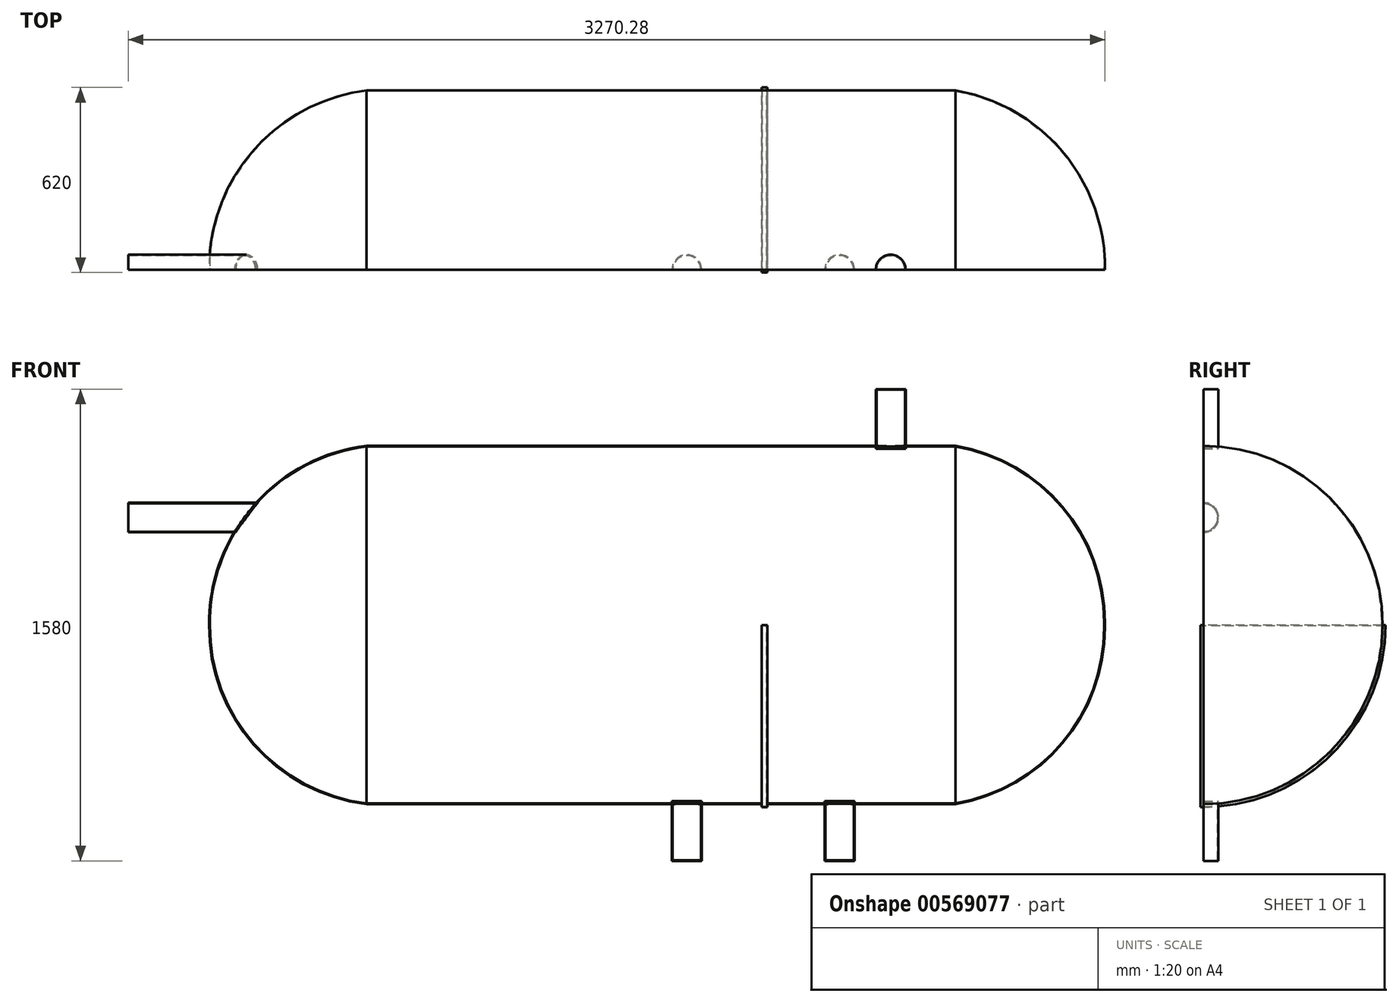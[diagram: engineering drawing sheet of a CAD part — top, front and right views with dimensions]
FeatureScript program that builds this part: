
annotation { "Feature Type Name" : "Feature", "Feature Type Description" : "" }
export const myFeature = defineFeature(function(context is Context, id is Id, definition is map)
    precondition{}
    {
        {
            var Q0;
            Q0=qCreatedBy(makeId("Front.planeOp"),FACE);
            var sketch = newSketch(context, id + "F0", { "sketchPlane" : qUnion([Q0])});
            skLineSegment(sketch, "E0.bottom", {"start": v(500, 0) * mm, "end": v(2500, 0) * mm});
            skLineSegment(sketch, "E0.top", {"start": v(500, -600) * mm, "end": v(2500, -600) * mm});
            skArc(sketch, "E1", {"start": v(0, 0) * mm, "mid": v(149.32, -400.52) * mm, "end": v(527.38, -600) * mm});
            skArc(sketch, "E2", {"start": v(2500, -600) * mm, "mid": v(2861, -392.5) * mm, "end": v(3000, 0) * mm});
            skLineSegment(sketch, "E3", {"start": v(0, 0) * mm, "end": v(500, 0) * mm});
            skLineSegment(sketch, "E4", {"start": v(2500, 0) * mm, "end": v(3000, 0) * mm});
            skSolve(sketch);
        }
        {
            var Q0;
            Q0 = qSketchRegion(id + "F0", true);
            var Q1;
            Q1=sQuery(id+"F0.wireOp",EDGE,"E0.bottom");
            revolve(context, id + "F1", {"entities" : qUnion([Q0]), "axis" : qUnion([Q1]), "revolveType" : RevolveType.ONE_DIRECTION, "angle" : 180 * degree});
        }
        {
            var Q0;
            Q0=makeQuery(id+"F1.opRevolve","CAP_FACE",FACE,{"disambiguationData":[OSD([sQuery(id+"F0.wireOp",EDGE,"E0.bottom"),sQuery(id+"F0.wireOp",EDGE,"E0.top"),sQuery(id+"F0.wireOp",EDGE,"E1"),sQuery(id+"F0.wireOp",EDGE,"E2"),sQuery(id+"F0.wireOp",EDGE,"E3"),sQuery(id+"F0.wireOp",EDGE,"E4")])],"isStart":false});
            shell(context, id + "F2", {"entities" : qUnion([Q0]), "thickness" : 2.5 * mm});
        }
        {
            var Q0;
            Q0=qCreatedBy(makeId("Front.planeOp"),FACE);
            var sketch = newSketch(context, id + "F3", { "sketchPlane" : qUnion([Q0])});
            skLineSegment(sketch, "E5", {"start": v(170.95, 360) * mm, "end": v(-279.05, 360) * mm});
            skArc(sketch, "E6", {"start": v(-420, 500) * mm, "mid": v(-378.38, 400.95) * mm, "end": v(-279.05, 360) * mm});
            skLineSegment(sketch, "E7", {"start": v(-420, 500) * mm, "end": v(-420, 900) * mm});
            skSolve(sketch);
        }
        {
            var Q0;
            Q0=qCreatedBy(makeId("Top.planeOp"),FACE);
            cPlane(context, id + "F4", {"entities" : qUnion([Q0]), "cplaneType" : CPlaneType.OFFSET, "offset" : 900 * mm, "width" : 150 * mm, "height" : 150 * mm});
        }
        {
            var Q0;
            Q0=qCreatedBy(id+"F4.planeOp",FACE);
            var sketch = newSketch(context, id + "F5", { "sketchPlane" : qUnion([Q0])});
            skCircle(sketch, "E8", {"center": v(-420, 0) * mm, "radius": 50 * mm});
            skSolve(sketch);
        }
        {
            var Q0;
            Q0=makeQuery(id+"F5.imprint","IMPRINT",FACE,{"disambiguationData":[TD([[makeQuery(id+"F5.imprint","IMPRINT",EDGE,{"derivedFrom":sQuery(id+"F5.wireOp",EDGE,"E8")}),1.0]])]});
            var Q1;
            Q1 = qConstructionFilter(qBodyType(qCreatedBy(id + "F3" ,EDGE), BodyType.WIRE), ConstructionObject.NO);
            sweep(context, id + "F6", {"profiles" : qUnion([Q0]), "path" : qUnion([Q1])});
        }
        {
            var Q0;
            Q0=qCreatedBy(makeId("Front.planeOp"),FACE);
            var sketch = newSketch(context, id + "F7", { "sketchPlane" : qUnion([Q0])});
            skLineSegment(sketch, "E9.bottom", {"start": v(1850, -610) * mm, "end": v(1870, -610) * mm});
            skLineSegment(sketch, "E9.top", {"start": v(1850, 0) * mm, "end": v(1870, 0) * mm});
            skLineSegment(sketch, "E9.left", {"start": v(1850, -610) * mm, "end": v(1850, 0) * mm});
            skLineSegment(sketch, "E9.right", {"start": v(1870, -610) * mm, "end": v(1870, 0) * mm});
            skSolve(sketch);
        }
        {
            var Q0;
            Q0 = qSketchRegion(id + "F7", true);
            var Q1;
            Q1=sQuery(id+"F7.wireOp",EDGE,"E9.top");
            revolve(context, id + "F8", {"operationType" : NewBodyOperationType.ADD, "entities" : qUnion([Q0]), "axis" : qUnion([Q1]), "revolveType" : RevolveType.ONE_DIRECTION, "angle" : 90 * degree});
        }
        {
            var Q0;
            Q0=makeQuery(id+"F66TGwe3fEh8Ifu_1.boolean.opBoolean","MERGE",FACE,{"derivedFrom":[makeQuery(id+"F8.boolean.opBoolean","MERGE",FACE,{"derivedFrom":[makeQuery(id+"F1.opRevolve","CAP_FACE",FACE,{"disambiguationData":[OSD([sQuery(id+"F0.wireOp",EDGE,"E0.bottom"),sQuery(id+"F0.wireOp",EDGE,"E0.top"),sQuery(id+"F0.wireOp",EDGE,"E1"),sQuery(id+"F0.wireOp",EDGE,"E2"),sQuery(id+"F0.wireOp",EDGE,"E3"),sQuery(id+"F0.wireOp",EDGE,"E4")])],"isStart":false}),makeQuery(id+"F8.opRevolve","CAP_FACE",FACE,{"disambiguationData":[OSD([sQuery(id+"F7.wireOp",EDGE,"E9.bottom"),sQuery(id+"F7.wireOp",EDGE,"E9.top"),sQuery(id+"F7.wireOp",EDGE,"E9.left"),sQuery(id+"F7.wireOp",EDGE,"E9.right")])],"isStart":true})]}),makeQuery(id+"F66TGwe3fEh8Ifu_1.opExtrude","CAP_FACE",FACE,{"disambiguationData":[OSD([sQuery(id+"FwUeZOf4pXkqyWq_1.wireOp",EDGE,"cfLgTzSa-ifk0-79PM-MiWR-QQtcIMDqkhwK.bottom"),sQuery(id+"FwUeZOf4pXkqyWq_1.wireOp",EDGE,"cfLgTzSa-ifk0-79PM-MiWR-QQtcIMDqkhwK.top"),sQuery(id+"FwUeZOf4pXkqyWq_1.wireOp",EDGE,"cfLgTzSa-ifk0-79PM-MiWR-QQtcIMDqkhwK.left"),sQuery(id+"FwUeZOf4pXkqyWq_1.wireOp",EDGE,"cfLgTzSa-ifk0-79PM-MiWR-QQtcIMDqkhwK.right")])],"isStart":true})]});
            shell(context, id + "F9", {"entities" : qUnion([Q0]), "thickness" : 2.5 * mm});
        }
        {
            var Q0;
            Q0=qCreatedBy(makeId("Front.planeOp"),FACE);
            var sketch = newSketch(context, id + "F10", { "sketchPlane" : qUnion([Q0])});
            skLineSegment(sketch, "E10.bottom", {"start": v(1600.1, -590) * mm, "end": v(1550.1, -590) * mm});
            skLineSegment(sketch, "E10.top", {"start": v(1600.1, -790) * mm, "end": v(1550.1, -790) * mm});
            skLineSegment(sketch, "E10.left", {"start": v(1600.1, -590) * mm, "end": v(1600.1, -790) * mm});
            skLineSegment(sketch, "E10.right", {"start": v(1550.1, -590) * mm, "end": v(1550.1, -790) * mm});
            skSolve(sketch);
        }
        {
            var Q0;
            Q0=qCreatedBy(makeId("Front.planeOp"),FACE);
            var sketch = newSketch(context, id + "F11", { "sketchPlane" : qUnion([Q0])});
            skLineSegment(sketch, "E11.bottom", {"start": v(2111.48, -590) * mm, "end": v(2161.48, -590) * mm});
            skLineSegment(sketch, "E11.top", {"start": v(2111.48, -790) * mm, "end": v(2161.48, -790) * mm});
            skLineSegment(sketch, "E11.left", {"start": v(2111.48, -590) * mm, "end": v(2111.48, -790) * mm});
            skLineSegment(sketch, "E11.right", {"start": v(2161.48, -590) * mm, "end": v(2161.48, -790) * mm});
            skSolve(sketch);
        }
        {
            var Q0;
            Q0=makeQuery(id+"F10.imprint","IMPRINT",FACE,{"disambiguationData":[TD([[makeQuery(id+"F10.imprint","IMPRINT",EDGE,{"derivedFrom":sQuery(id+"F10.wireOp",EDGE,"E10.bottom")}),1.0]])]});
            var Q1;
            Q1=sQuery(id+"F10.wireOp",EDGE,"E10.left");
            revolve(context, id + "F12", {"entities" : qUnion([Q0]), "axis" : qUnion([Q1]), "revolveType" : RevolveType.FULL});
        }
        {
            var Q0;
            Q0 = qSketchRegion(id + "F11", true);
            var Q1;
            Q1=sQuery(id+"F11.wireOp",EDGE,"E11.left");
            revolve(context, id + "F13", {"entities" : qUnion([Q0]), "axis" : qUnion([Q1]), "revolveType" : RevolveType.FULL});
        }
        {
            var Q0;
            Q0=qCreatedBy(makeId("Front.planeOp"),FACE);
            var sketch = newSketch(context, id + "F14", { "sketchPlane" : qUnion([Q0])});
            skLineSegment(sketch, "E12.bottom", {"start": v(1156.03, 0) * mm, "end": v(2681.67, 0) * mm});
            skLineSegment(sketch, "E12.top", {"start": v(1156.03, -1019.93) * mm, "end": v(2681.67, -1019.93) * mm});
            skLineSegment(sketch, "E12.left", {"start": v(1156.03, 0) * mm, "end": v(1156.03, -1019.93) * mm});
            skLineSegment(sketch, "E12.right", {"start": v(2681.67, 0) * mm, "end": v(2681.67, -1019.93) * mm});
            skSolve(sketch);
        }
        {
            var Q0;
            Q0 = qSketchRegion(id + "F14", true);
            extrude(context, id + "F15", {"entities" : qUnion([Q0]), "operationType" : NewBodyOperationType.REMOVE, "depth" : 1000 * mm, "offsetDistance" : 25 * mm});
        }
        {
            var Q0;
            Q0=qCreatedBy(makeId("Front.planeOp"),FACE);
            var sketch = newSketch(context, id + "F16", { "sketchPlane" : qUnion([Q0])});
            skLineSegment(sketch, "E13.bottom", {"start": v(2282.6, 590) * mm, "end": v(2232.6, 590) * mm});
            skLineSegment(sketch, "E13.top", {"start": v(2282.6, 790) * mm, "end": v(2232.6, 790) * mm});
            skLineSegment(sketch, "E13.left", {"start": v(2282.6, 590) * mm, "end": v(2282.6, 790) * mm});
            skLineSegment(sketch, "E13.right", {"start": v(2232.6, 590) * mm, "end": v(2232.6, 790) * mm});
            skSolve(sketch);
        }
        {
            var Q0;
            Q0=makeQuery(id+"F16.imprint","IMPRINT",FACE,{"disambiguationData":[TD([[makeQuery(id+"F16.imprint","IMPRINT",EDGE,{"derivedFrom":sQuery(id+"F16.wireOp",EDGE,"E13.bottom")}),-1.0]])]});
            var Q1;
            Q1=sQuery(id+"F16.wireOp",EDGE,"E13.left");
            revolve(context, id + "F17", {"entities" : qUnion([Q0]), "axis" : qUnion([Q1]), "revolveType" : RevolveType.FULL});
        }
        {
            var Q0;
            Q0=qCreatedBy(makeId("Front.planeOp"),FACE);
            var sketch = newSketch(context, id + "F18", { "sketchPlane" : qUnion([Q0])});
            skLineSegment(sketch, "E14.bottom", {"start": v(1632.95, 124.35) * mm, "end": v(2557.46, 124.35) * mm});
            skLineSegment(sketch, "E14.top", {"start": v(1632.95, 1072.21) * mm, "end": v(2557.46, 1072.21) * mm});
            skLineSegment(sketch, "E14.left", {"start": v(1632.95, 124.35) * mm, "end": v(1632.95, 1072.21) * mm});
            skLineSegment(sketch, "E14.right", {"start": v(2557.46, 124.35) * mm, "end": v(2557.46, 1072.21) * mm});
            skSolve(sketch);
        }
        {
            var Q0;
            Q0 = qSketchRegion(id + "F18", true);
            extrude(context, id + "F19", {"entities" : qUnion([Q0]), "operationType" : NewBodyOperationType.REMOVE, "depth" : 500 * mm, "offsetDistance" : 25 * mm});
        }
        {
            var Q0;
            Q0=makeQuery(id+"F15.boolean.opBoolean","COPY",FACE,{"disambiguationData":[TD([makeQuery(id+"F12.opRevolve","SWEPT_FACE",FACE,{"disambiguationData":[OSD([sQuery(id+"F10.wireOp",EDGE,"E10.bottom")])]})])],"derivedFrom":makeQuery(id+"F15.opExtrude","CAP_FACE",FACE,{"disambiguationData":[OSD([sQuery(id+"F14.wireOp",EDGE,"E12.bottom"),sQuery(id+"F14.wireOp",EDGE,"E12.top"),sQuery(id+"F14.wireOp",EDGE,"E12.left"),sQuery(id+"F14.wireOp",EDGE,"E12.right")])],"isStart":true})});
            shell(context, id + "F20", {"entities" : qUnion([Q0]), "thickness" : 2.5 * mm});
        }
        {
            var Q0;
            Q0=makeQuery(id+"F15.boolean.opBoolean","COPY",FACE,{"disambiguationData":[TD([makeQuery(id+"F13.opRevolve","SWEPT_FACE",FACE,{"disambiguationData":[OSD([sQuery(id+"F11.wireOp",EDGE,"E11.bottom")])]})])],"derivedFrom":makeQuery(id+"F15.opExtrude","CAP_FACE",FACE,{"disambiguationData":[OSD([sQuery(id+"F14.wireOp",EDGE,"E12.bottom"),sQuery(id+"F14.wireOp",EDGE,"E12.top"),sQuery(id+"F14.wireOp",EDGE,"E12.left"),sQuery(id+"F14.wireOp",EDGE,"E12.right")])],"isStart":true})});
            shell(context, id + "F21", {"entities" : qUnion([Q0]), "thickness" : 2.5 * mm});
        }
        {
            var Q0;
            Q0=makeQuery(id+"F19.boolean.opBoolean","COPY",FACE,{"derivedFrom":makeQuery(id+"F19.opExtrude","CAP_FACE",FACE,{"disambiguationData":[OSD([sQuery(id+"F18.wireOp",EDGE,"E14.bottom"),sQuery(id+"F18.wireOp",EDGE,"E14.top"),sQuery(id+"F18.wireOp",EDGE,"E14.left"),sQuery(id+"F18.wireOp",EDGE,"E14.right")])],"isStart":true})});
            shell(context, id + "F22", {"entities" : qUnion([Q0]), "thickness" : 2.5 * mm});
        }
        {
            var Q0;
            Q0=qCreatedBy(makeId("Front.planeOp"),FACE);
            var sketch = newSketch(context, id + "F23", { "sketchPlane" : qUnion([Q0])});
            skLineSegment(sketch, "E15.bottom", {"start": v(-920.74, -263.75) * mm, "end": v(1158.3, -263.75) * mm});
            skLineSegment(sketch, "E15.top", {"start": v(-920.74, 1325.57) * mm, "end": v(1158.3, 1325.57) * mm});
            skLineSegment(sketch, "E15.left", {"start": v(-920.74, -263.75) * mm, "end": v(-920.74, 1325.57) * mm});
            skLineSegment(sketch, "E15.right", {"start": v(1158.3, -263.75) * mm, "end": v(1158.3, 1325.57) * mm});
            skSolve(sketch);
        }
        {
            var Q0;
            Q0=makeQuery(id+"F23.imprint","IMPRINT",FACE,{"disambiguationData":[TD([[makeQuery(id+"F23.imprint","IMPRINT",EDGE,{"derivedFrom":sQuery(id+"F23.wireOp",EDGE,"E15.bottom")}),1.0]])]});
            extrude(context, id + "F24", {"entities" : qUnion([Q0]), "operationType" : NewBodyOperationType.REMOVE, "depth" : 500 * mm, "offsetDistance" : 25 * mm});
        }
        {
            var Q0;
            Q0=makeQuery(id+"F24.boolean.opBoolean","COPY",FACE,{"derivedFrom":makeQuery(id+"F24.opExtrude","CAP_FACE",FACE,{"disambiguationData":[OSD([sQuery(id+"F23.wireOp",EDGE,"E15.bottom"),sQuery(id+"F23.wireOp",EDGE,"E15.top"),sQuery(id+"F23.wireOp",EDGE,"E15.left"),sQuery(id+"F23.wireOp",EDGE,"E15.right")])],"isStart":true})});
            shell(context, id + "F25", {"entities" : qUnion([Q0]), "thickness" : 2.5 * mm});
        }
        {
            var Q0;
            Q0=makeQuery(id+"F6.opSweep","CAP_FACE",FACE,{"disambiguationData":[OSD([sQuery(id+"F3.wireOp",VERTEX,"E5.start"),sQuery(id+"F5.wireOp",EDGE,"E8")])],"isStart":false});
            var sketch = newSketch(context, id + "F26", { "sketchPlane" : qUnion([Q0])});
            skArc(sketch, "E16", {"start": v(0, 313) * mm, "mid": v(47, 360) * mm, "end": v(0, 407) * mm});
            skLineSegment(sketch, "E17", {"start": v(0, 407) * mm, "end": v(0, 313) * mm});
            skSolve(sketch);
        }
        {
            var Q0;
            Q0 = qSketchRegion(id + "F26", true);
            extrude(context, id + "F27", {"entities" : qUnion([Q0]), "operationType" : NewBodyOperationType.REMOVE, "oppositeDirection" : true, "depth" : 200 * mm, "offsetDistance" : 25 * mm});
        }
        {
            var Q0;
            Q0=makeQuery(id+"F20.opShell","OFFSET_FACE",FACE,{"disambiguationData":[OSD([sQuery(id+"F10.wireOp",EDGE,"E10.top")])]});
            var sketch = newSketch(context, id + "F28", { "sketchPlane" : qUnion([Q0])});
            skArc(sketch, "E18", {"start": v(1647.1, 0) * mm, "mid": v(1600.1, 47) * mm, "end": v(1553.1, 0) * mm});
            skLineSegment(sketch, "E19", {"start": v(1647.1, 0) * mm, "end": v(1553.1, 0) * mm});
            skSolve(sketch);
        }
        {
            var Q0;
            Q0 = qSketchRegion(id + "F28", true);
            extrude(context, id + "F29", {"entities" : qUnion([Q0]), "operationType" : NewBodyOperationType.REMOVE, "depth" : 500 * mm, "offsetDistance" : 25 * mm});
        }
        {
            var Q0;
            Q0=makeQuery(id+"F21.opShell","OFFSET_FACE",FACE,{"disambiguationData":[OSD([sQuery(id+"F11.wireOp",EDGE,"E11.top")])]});
            var sketch = newSketch(context, id + "F30", { "sketchPlane" : qUnion([Q0])});
            skArc(sketch, "E20", {"start": v(2158.48, 0) * mm, "mid": v(2111.48, 47) * mm, "end": v(2064.48, 0) * mm});
            skLineSegment(sketch, "E21", {"start": v(2158.48, 0) * mm, "end": v(2064.48, 0) * mm});
            skSolve(sketch);
        }
        {
            var Q0;
            Q0 = qSketchRegion(id + "F30", true);
            extrude(context, id + "F31", {"entities" : qUnion([Q0]), "operationType" : NewBodyOperationType.REMOVE, "depth" : 500 * mm, "offsetDistance" : 25 * mm});
        }
        {
            var Q0;
            Q0=makeQuery(id+"F22.opShell","OFFSET_FACE",FACE,{"disambiguationData":[OSD([sQuery(id+"F16.wireOp",EDGE,"E13.top")])]});
            var sketch = newSketch(context, id + "F32", { "sketchPlane" : qUnion([Q0])});
            skArc(sketch, "E22", {"start": v(2235.6, 0) * mm, "mid": v(2282.6, -47) * mm, "end": v(2329.6, 0) * mm});
            skLineSegment(sketch, "E23", {"start": v(2329.6, 0) * mm, "end": v(2235.6, 0) * mm});
            skSolve(sketch);
        }
        {
            var Q0;
            Q0 = qSketchRegion(id + "F32", true);
            extrude(context, id + "F33", {"entities" : qUnion([Q0]), "operationType" : NewBodyOperationType.REMOVE, "depth" : 500 * mm, "offsetDistance" : 25 * mm});
        }
        {
            var Q0;
            Q0=qCreatedBy(makeId("Front.planeOp"),FACE);
            var sketch = newSketch(context, id + "F34", { "sketchPlane" : qUnion([Q0])});
            skLineSegment(sketch, "E24.bottom", {"start": v(-656.16, 1025.44) * mm, "end": v(-270.22, 1025.44) * mm});
            skLineSegment(sketch, "E24.top", {"start": v(-656.16, 80.4) * mm, "end": v(-270.22, 80.4) * mm});
            skLineSegment(sketch, "E24.left", {"start": v(-656.16, 1025.44) * mm, "end": v(-656.16, 80.4) * mm});
            skLineSegment(sketch, "E24.right", {"start": v(-270.22, 1025.44) * mm, "end": v(-270.22, 80.4) * mm});
            skSolve(sketch);
        }
        {
            var Q0;
            Q0 = qSketchRegion(id + "F34", true);
            extrude(context, id + "F35", {"entities" : qUnion([Q0]), "operationType" : NewBodyOperationType.REMOVE, "endBound" : BoundingType.SYMMETRIC, "depth" : 500 * mm, "offsetDistance" : 25 * mm});
        }
        {
            var Q0;
            Q0=makeQuery(id+"F0.imprint","IMPRINT",FACE,{"disambiguationData":[TD([[makeQuery(id+"F0.imprint","IMPRINT",EDGE,{"derivedFrom":sQuery(id+"F0.wireOp",EDGE,"E0.bottom")}),-1.0]])]});
            var sketch = newSketch(context, id + "F36", { "sketchPlane" : qUnion([Q0])});
            skArc(sketch, "E25", {"start": v(3, 0) * mm, "mid": v(152.24, -397.77) * mm, "end": v(527.48, -597) * mm});
            skLineSegment(sketch, "E26", {"start": v(3, 0) * mm, "end": v(527.1, 0) * mm});
            skLineSegment(sketch, "E27", {"start": v(527.1, 0) * mm, "end": v(527.48, -597) * mm});
            skSolve(sketch);
        }
        {
            var Q0;
            Q0 = qSketchRegion(id + "F36", true);
            var Q1;
            Q1=sQuery(id+"F36.wireOp",EDGE,"E26");
            revolve(context, id + "F37", {"operationType" : NewBodyOperationType.REMOVE, "entities" : qUnion([Q0]), "axis" : qUnion([Q1]), "revolveType" : RevolveType.FULL, "oppositeDirection" : true});
        }
        {
            var Q0;
            Q0 = qSketchRegion(id + "F7", true);
            extrude(context, id + "F38", {"entities" : qUnion([Q0]), "operationType" : NewBodyOperationType.ADD, "depth" : 10 * mm, "offsetDistance" : 25 * mm});
        }
    });
